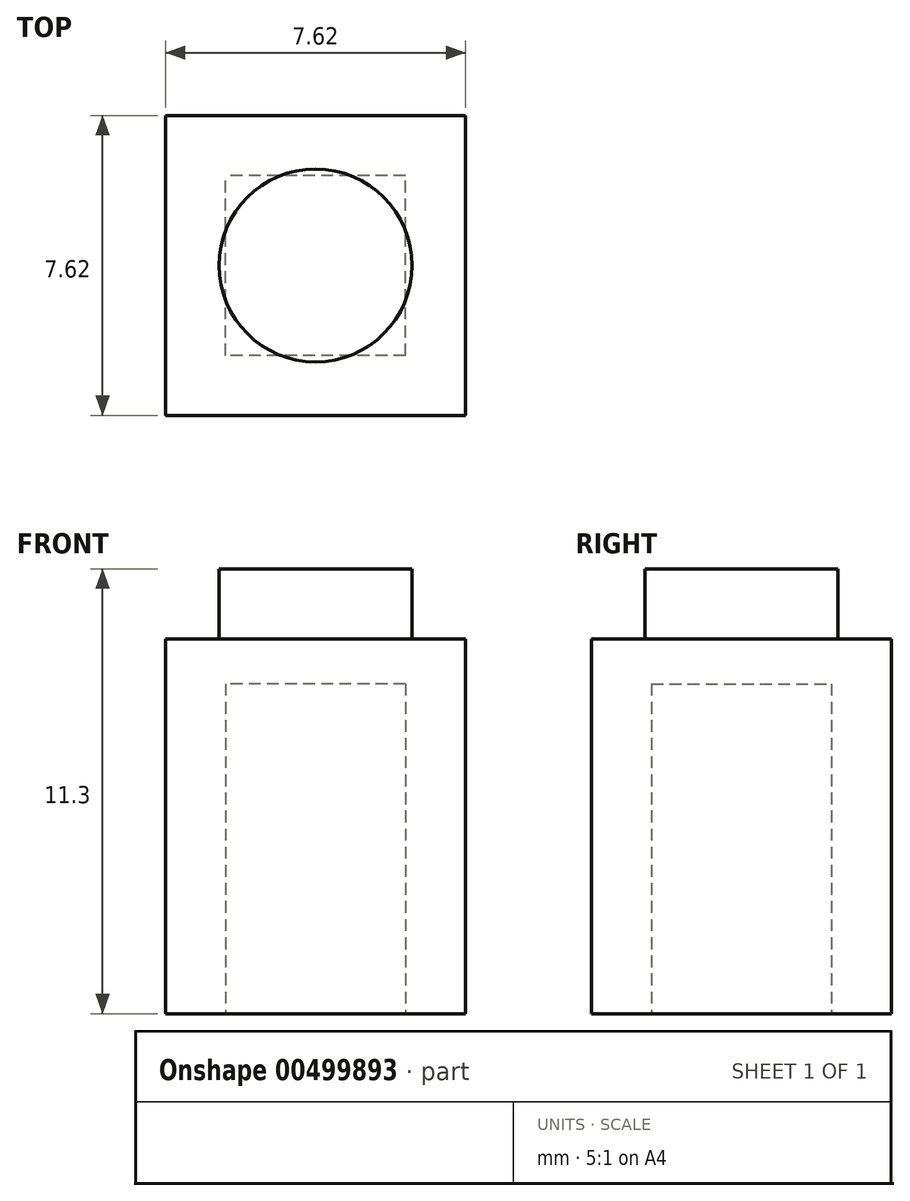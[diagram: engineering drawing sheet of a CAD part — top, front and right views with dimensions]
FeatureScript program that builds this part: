
annotation { "Feature Type Name" : "Feature", "Feature Type Description" : "" }
export const myFeature = defineFeature(function(context is Context, id is Id, definition is map)
    precondition{}
    {
        {
            var Q0;
            Q0=qCreatedBy(makeId("Top.planeOp"),FACE);
            var sketch = newSketch(context, id + "F0", { "sketchPlane" : qUnion([Q0])});
            skLineSegment(sketch, "E0.bottom", {"start": v(3.8, 3.81) * mm, "end": v(-3.8, 3.81) * mm});
            skLineSegment(sketch, "E0.top", {"start": v(3.8, -3.81) * mm, "end": v(-3.8, -3.81) * mm});
            skLineSegment(sketch, "E0.left", {"start": v(3.81, 3.81) * mm, "end": v(3.81, -3.81) * mm});
            skLineSegment(sketch, "E0.right", {"start": v(-3.81, 3.81) * mm, "end": v(-3.81, -3.81) * mm});
            skPoint(sketch, "E0.middle", {"position": v(0, 0) * mm});
            skSolve(sketch);
        }
        {
            var Q0;
            Q0=makeQuery(id+"F0.imprint","IMPRINT",FACE,{"disambiguationData":[TD([[makeQuery(id+"F0.imprint","IMPRINT",EDGE,{"derivedFrom":sQuery(id+"F0.wireOp",EDGE,"E0.bottom")}),1.0]])]});
            extrude(context, id + "F1", {"entities" : qUnion([Q0]), "endBound" : BoundingType.SYMMETRIC, "depth" : 9.52 * mm});
        }
        {
            var Q0;
            Q0=makeQuery(id+"F1.opExtrude","CAP_FACE",FACE,{"disambiguationData":[OSD([sQuery(id+"F0.wireOp",EDGE,"E0.bottom"),sQuery(id+"F0.wireOp",EDGE,"E0.top"),sQuery(id+"F0.wireOp",EDGE,"E0.left"),sQuery(id+"F0.wireOp",EDGE,"E0.right")])],"isStart":false});
            var sketch = newSketch(context, id + "F2", { "sketchPlane" : qUnion([Q0])});
            skCircle(sketch, "E1", {"center": v(0, 0) * mm, "radius": 2.45 * mm});
            skSolve(sketch);
        }
        {
            var Q0;
            Q0=makeQuery(id+"F2.imprint","IMPRINT",FACE,{"disambiguationData":[TD([[makeQuery(id+"F2.imprint","IMPRINT",EDGE,{"derivedFrom":sQuery(id+"F2.wireOp",EDGE,"E1")}),1.0]])]});
            extrude(context, id + "F3", {"entities" : qUnion([Q0]), "operationType" : NewBodyOperationType.ADD, "depth" : 1.78 * mm});
        }
        {
            var Q0;
            Q0=makeQuery(id+"F1.opExtrude","CAP_FACE",FACE,{"disambiguationData":[OSD([sQuery(id+"F0.wireOp",EDGE,"E0.bottom"),sQuery(id+"F0.wireOp",EDGE,"E0.top"),sQuery(id+"F0.wireOp",EDGE,"E0.left"),sQuery(id+"F0.wireOp",EDGE,"E0.right")])],"isStart":true});
            var sketch = newSketch(context, id + "F4", { "sketchPlane" : qUnion([Q0])});
            skLineSegment(sketch, "E2.bottom", {"start": v(2.29, 2.29) * mm, "end": v(-2.29, 2.29) * mm});
            skLineSegment(sketch, "E2.top", {"start": v(2.29, -2.29) * mm, "end": v(-2.29, -2.29) * mm});
            skLineSegment(sketch, "E2.left", {"start": v(2.29, 2.29) * mm, "end": v(2.29, -2.29) * mm});
            skLineSegment(sketch, "E2.right", {"start": v(-2.29, 2.29) * mm, "end": v(-2.29, -2.29) * mm});
            skPoint(sketch, "E2.middle", {"position": v(0, 0) * mm});
            skSolve(sketch);
        }
        {
            var Q0;
            Q0=makeQuery(id+"F4.imprint","IMPRINT",FACE,{"disambiguationData":[TD([[makeQuery(id+"F4.imprint","IMPRINT",EDGE,{"derivedFrom":sQuery(id+"F4.wireOp",EDGE,"E2.bottom")}),1.0]])]});
            extrude(context, id + "F5", {"entities" : qUnion([Q0]), "operationType" : NewBodyOperationType.REMOVE, "oppositeDirection" : true, "depth" : 8.38 * mm});
        }
    });
